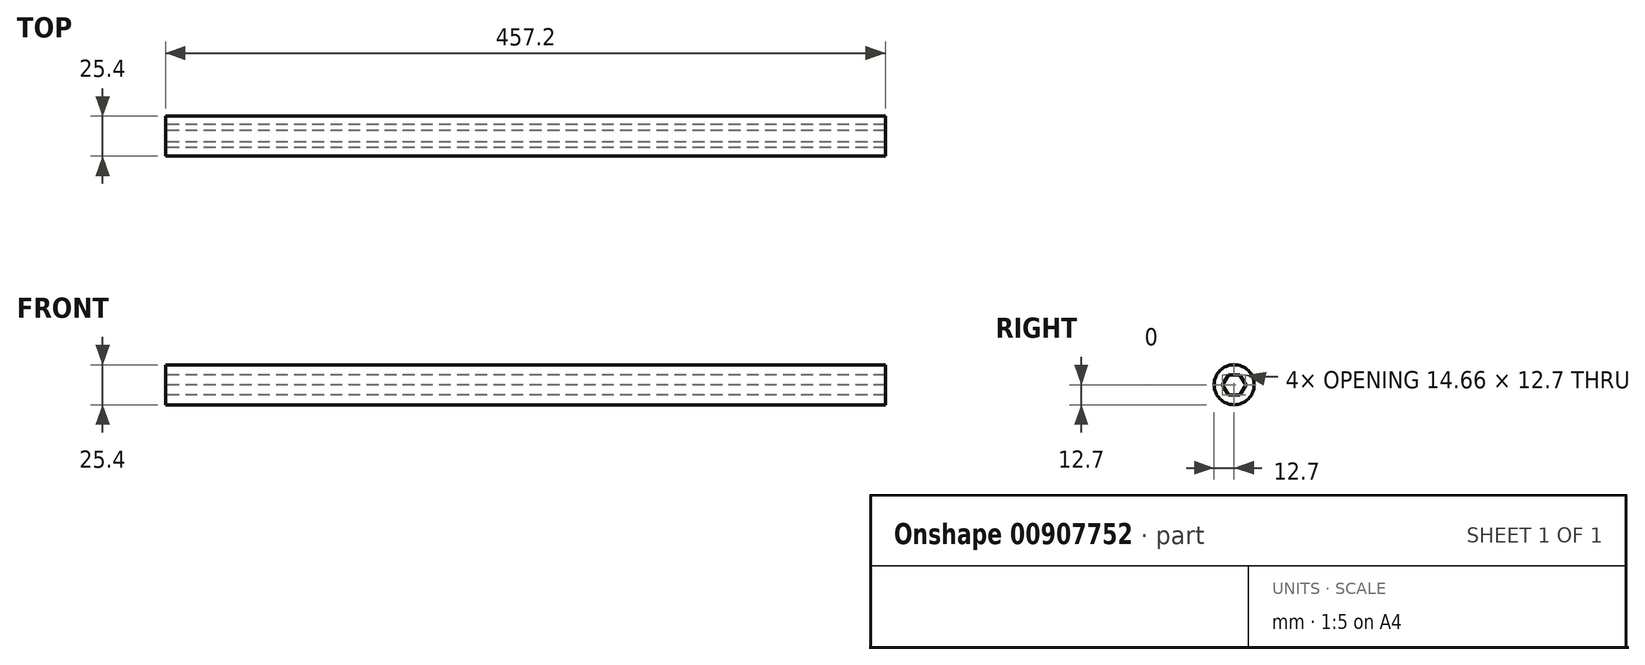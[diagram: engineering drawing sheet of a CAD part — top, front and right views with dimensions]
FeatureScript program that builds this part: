
annotation { "Feature Type Name" : "Feature", "Feature Type Description" : "" }
export const myFeature = defineFeature(function(context is Context, id is Id, definition is map)
    precondition{}
    {
        {
            var Q0;
            Q0=qCreatedBy(makeId("Right.planeOp"),FACE);
            var sketch = newSketch(context, id + "F0", { "sketchPlane" : qUnion([Q0])});
            skCircle(sketch, "E0", {"center": v(0, 0) * mm, "radius": 12.7 * mm});
            skCircle(sketch, "E1.cCircle", {"center": v(0, 0) * mm, "radius": 6.35 * mm, "construction": true});
            skLineSegment(sketch, "E1.0", {"start": v(3.67, 6.35) * mm, "end": v(7.33, 0) * mm});
            skLineSegment(sketch, "E1.1", {"start": v(7.33, 0) * mm, "end": v(3.66, -6.35) * mm});
            skLineSegment(sketch, "E1.2", {"start": v(3.66, -6.35) * mm, "end": v(-3.67, -6.35) * mm});
            skLineSegment(sketch, "E1.3", {"start": v(-3.67, -6.35) * mm, "end": v(-7.33, 0) * mm});
            skLineSegment(sketch, "E1.4", {"start": v(-7.33, 0) * mm, "end": v(-3.66, 6.35) * mm});
            skLineSegment(sketch, "E1.5", {"start": v(-3.66, 6.35) * mm, "end": v(3.67, 6.35) * mm});
            skPoint(sketch, "E1.0.midPoint", {"position": v(5.5, 3.17) * mm});
            skSolve(sketch);
        }
        {
            var Q0;
            Q0 = qSketchRegion(id + "F0", true);
            extrude(context, id + "F1", {"entities" : qUnion([Q0]), "depth" : 457.2 * mm, "offsetDistance" : 25.4 * mm});
        }
    });
